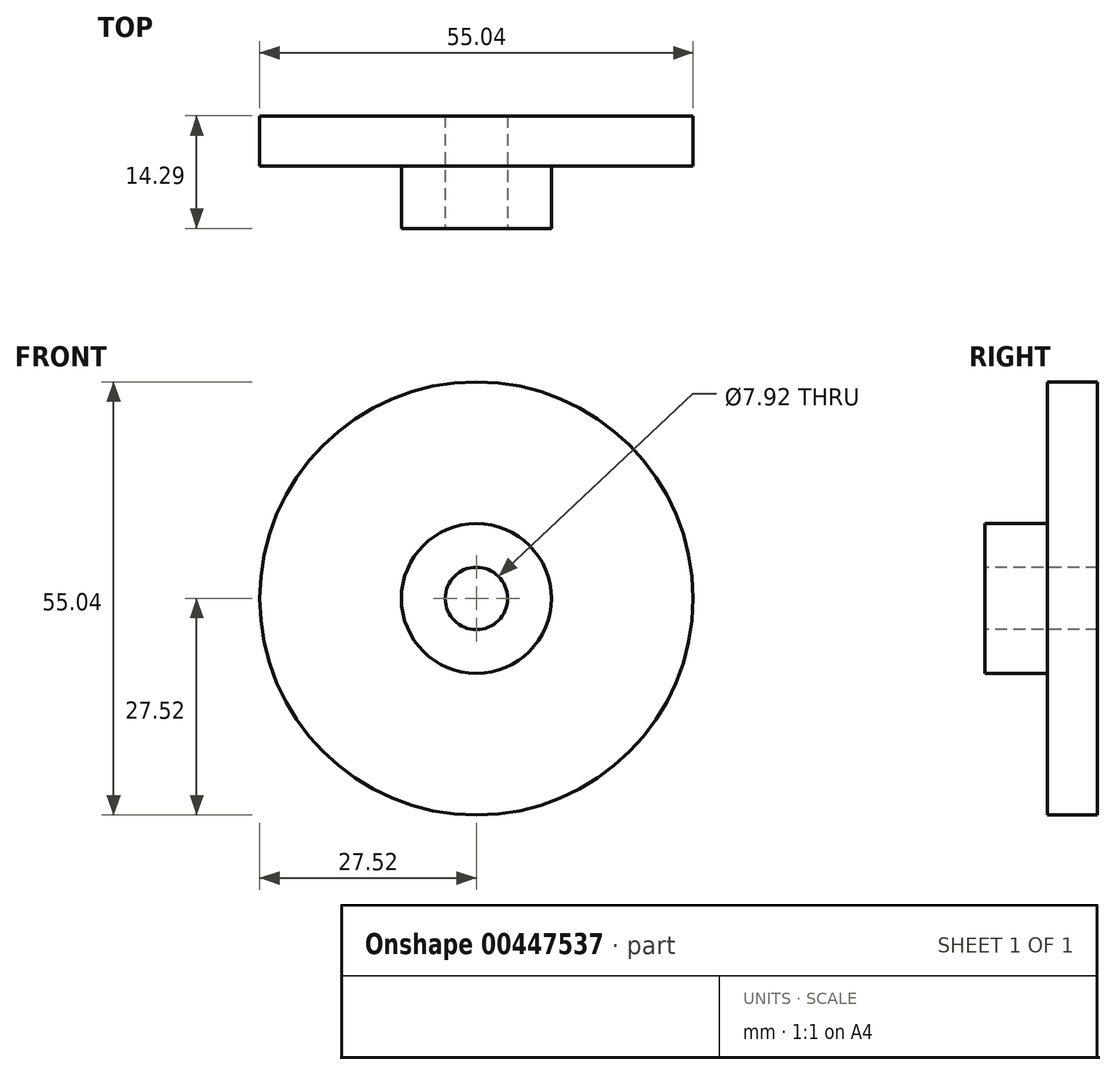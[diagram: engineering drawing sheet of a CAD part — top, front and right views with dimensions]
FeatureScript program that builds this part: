
annotation { "Feature Type Name" : "Feature", "Feature Type Description" : "" }
export const myFeature = defineFeature(function(context is Context, id is Id, definition is map)
    precondition{}
    {
        {
            var Q0;
            Q0=qCreatedBy(makeId("Front.planeOp"),FACE);
            var sketch = newSketch(context, id + "F0", { "sketchPlane" : qUnion([Q0])});
            skCircle(sketch, "E0", {"center": v(0, 0) * mm, "radius": 27.52 * mm});
            skSolve(sketch);
        }
        {
            var Q0;
            Q0=makeQuery(id+"F0.imprint","IMPRINT",FACE,{"disambiguationData":[TD([[makeQuery(id+"F0.imprint","IMPRINT",EDGE,{"derivedFrom":sQuery(id+"F0.wireOp",EDGE,"E0")}),1.0]])]});
            extrude(context, id + "F1", {"entities" : qUnion([Q0]), "oppositeDirection" : true, "depth" : 14.29 * mm});
        }
        {
            var Q0;
            Q0=makeQuery(id+"F1.opExtrude","CAP_FACE",FACE,{"disambiguationData":[OSD([sQuery(id+"F0.wireOp",EDGE,"E0")])],"isStart":true});
            var sketch = newSketch(context, id + "F2", { "sketchPlane" : qUnion([Q0])});
            skCircle(sketch, "E1", {"center": v(0, 0) * mm, "radius": 9.53 * mm});
            skCircle(sketch, "E2", {"center": v(0, 0) * mm, "radius": 27.52 * mm});
            skSolve(sketch);
        }
        {
            var Q0;
            Q0=makeQuery(id+"F2.imprint","IMPRINT",FACE,{"disambiguationData":[TD([[makeQuery(id+"F2.imprint","IMPRINT",EDGE,{"derivedFrom":sQuery(id+"F2.wireOp",EDGE,"E1")}),-1.0]])]});
            extrude(context, id + "F3", {"entities" : qUnion([Q0]), "operationType" : NewBodyOperationType.REMOVE, "oppositeDirection" : true, "depth" : 7.94 * mm});
        }
        {
            var Q0;
            Q0=makeQuery(id+"F1.opExtrude","CAP_FACE",FACE,{"disambiguationData":[OSD([sQuery(id+"F0.wireOp",EDGE,"E0")])],"isStart":true});
            var sketch = newSketch(context, id + "F4", { "sketchPlane" : qUnion([Q0])});
            skCircle(sketch, "E3", {"center": v(0, 0) * mm, "radius": 3.96 * mm});
            skSolve(sketch);
        }
        {
            var Q0;
            Q0=makeQuery(id+"F4.imprint","IMPRINT",FACE,{"disambiguationData":[TD([[makeQuery(id+"F4.imprint","IMPRINT",EDGE,{"derivedFrom":sQuery(id+"F4.wireOp",EDGE,"E3")}),1.0]])]});
            extrude(context, id + "F5", {"entities" : qUnion([Q0]), "operationType" : NewBodyOperationType.REMOVE, "endBound" : BoundingType.THROUGH_ALL, "oppositeDirection" : true, "depth" : 25.4 * mm});
        }
    });
